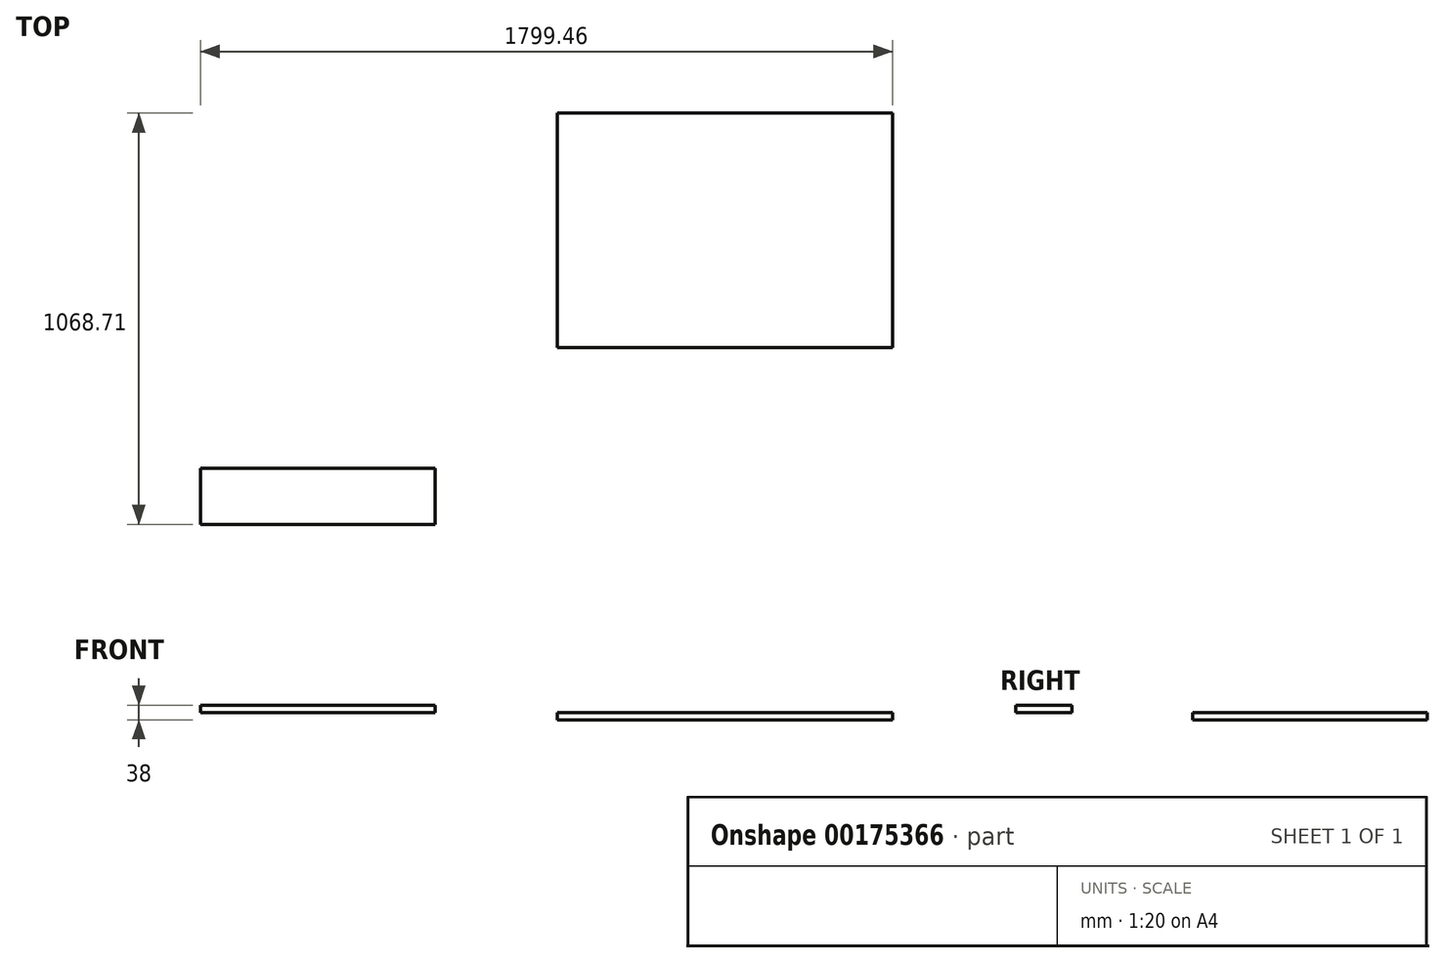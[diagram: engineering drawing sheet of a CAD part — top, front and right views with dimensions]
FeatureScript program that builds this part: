
annotation { "Feature Type Name" : "Feature", "Feature Type Description" : "" }
export const myFeature = defineFeature(function(context is Context, id is Id, definition is map)
    precondition{}
    {
        {
            var Q0;
            Q0=qCreatedBy(makeId("Top.planeOp"),FACE);
            var sketch = newSketch(context, id + "F0", { "sketchPlane" : qUnion([Q0])});
            skLineSegment(sketch, "E0.bottom", {"start": v(-421.12, 379.65) * mm, "end": v(450.88, 379.65) * mm});
            skLineSegment(sketch, "E0.top", {"start": v(-421.12, -230.35) * mm, "end": v(450.88, -230.35) * mm});
            skLineSegment(sketch, "E0.left", {"start": v(-421.12, 379.65) * mm, "end": v(-421.12, -230.35) * mm});
            skLineSegment(sketch, "E0.right", {"start": v(450.88, 379.65) * mm, "end": v(450.88, -230.35) * mm});
            skSolve(sketch);
        }
        {
            var Q0;
            Q0=makeQuery(id+"F0.imprint","IMPRINT",FACE,{"disambiguationData":[TD([[makeQuery(id+"F0.imprint","IMPRINT",EDGE,{"derivedFrom":sQuery(id+"F0.wireOp",EDGE,"E0.bottom")}),-1.0]])]});
            extrude(context, id + "F1", {"entities" : qUnion([Q0]), "depth" : 19 * mm});
        }
        {
            var Q0;
            Q0=makeQuery(id+"F1.opExtrude","CAP_FACE",FACE,{"disambiguationData":[OSD([sQuery(id+"F0.wireOp",EDGE,"E0.bottom"),sQuery(id+"F0.wireOp",EDGE,"E0.top"),sQuery(id+"F0.wireOp",EDGE,"E0.left"),sQuery(id+"F0.wireOp",EDGE,"E0.right")])],"isStart":false});
            var sketch = newSketch(context, id + "F2", { "sketchPlane" : qUnion([Q0])});
            skLineSegment(sketch, "E1.bottom", {"start": v(-1348.58, -544.06) * mm, "end": v(-738.58, -544.06) * mm});
            skLineSegment(sketch, "E1.top", {"start": v(-1348.58, -689.06) * mm, "end": v(-738.58, -689.06) * mm});
            skLineSegment(sketch, "E1.left", {"start": v(-1348.58, -544.06) * mm, "end": v(-1348.58, -689.06) * mm});
            skLineSegment(sketch, "E1.right", {"start": v(-738.58, -544.06) * mm, "end": v(-738.58, -689.06) * mm});
            skSolve(sketch);
        }
        {
            var Q0;
            Q0=makeQuery(id+"F2.imprint","IMPRINT",FACE,{"disambiguationData":[TD([[makeQuery(id+"F2.imprint","IMPRINT",EDGE,{"derivedFrom":sQuery(id+"F2.wireOp",EDGE,"E1.bottom")}),-1.0]])]});
            extrude(context, id + "F3", {"entities" : qUnion([Q0]), "depth" : 19 * mm});
        }
    });
